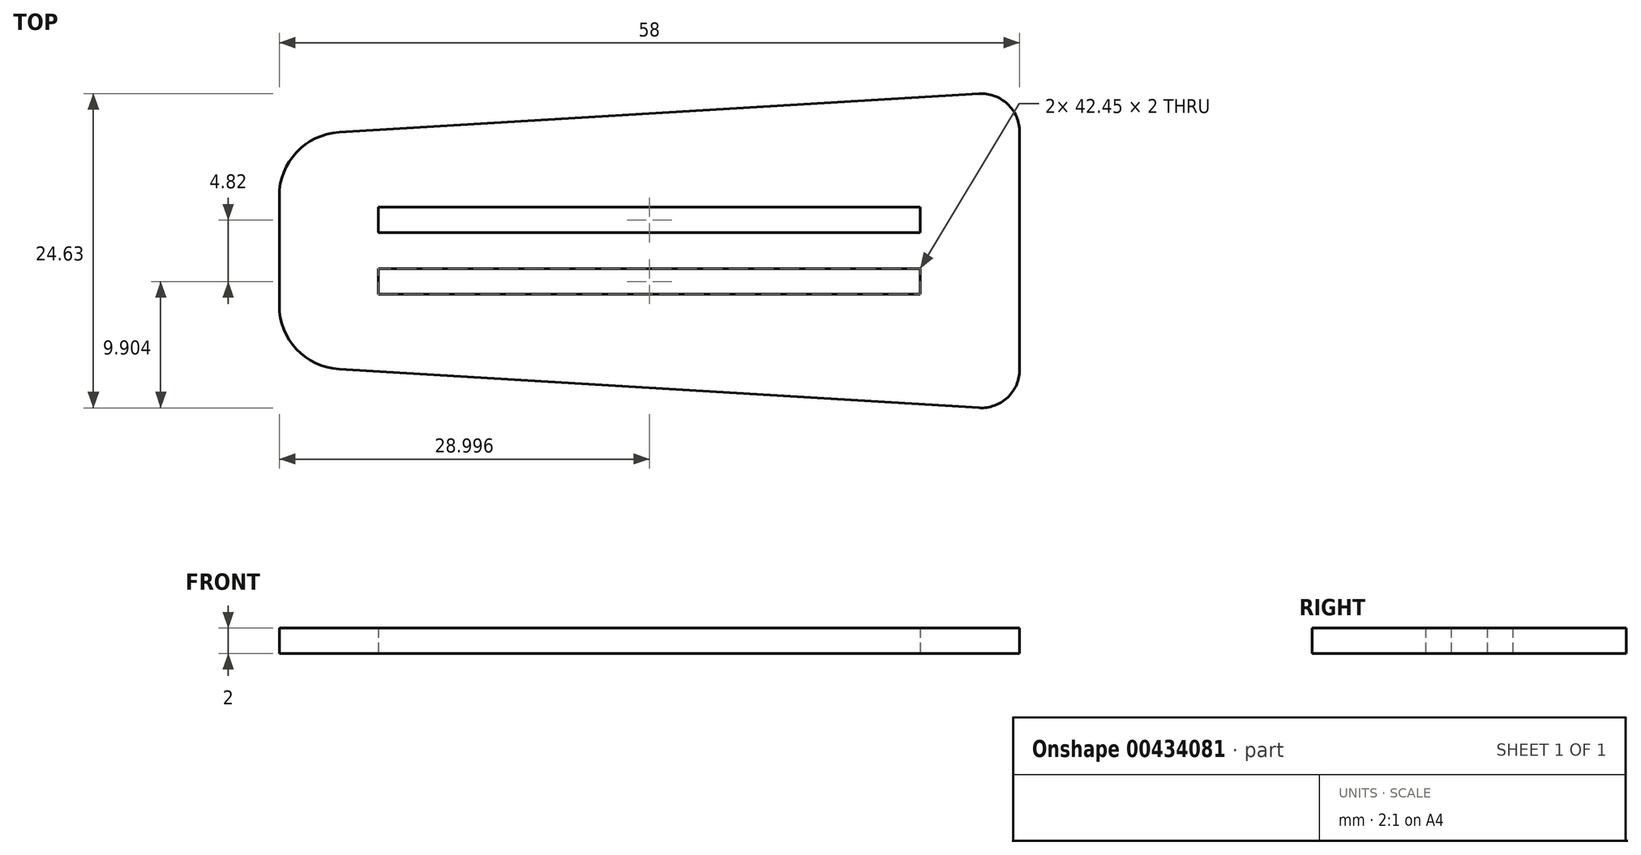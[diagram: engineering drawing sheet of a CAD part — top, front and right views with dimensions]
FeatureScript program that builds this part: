
annotation { "Feature Type Name" : "Feature", "Feature Type Description" : "" }
export const myFeature = defineFeature(function(context is Context, id is Id, definition is map)
    precondition{}
    {
        {
            var Q0;
            Q0=qCreatedBy(makeId("Top.planeOp"),FACE);
            var sketch = newSketch(context, id + "F0", { "sketchPlane" : qUnion([Q0])});
            skLineSegment(sketch, "E0.left", {"start": v(-65.71, 36.47) * mm, "end": v(-65.71, 33.65) * mm});
            skLineSegment(sketch, "E0.right", {"start": v(-7.71, 47.56) * mm, "end": v(-7.71, 22.56) * mm});
            skLineSegment(sketch, "E1", {"start": v(-81.04, 35.06) * mm, "end": v(-57.94, 35.06) * mm, "construction": true});
            skPoint(sketch, "E1.startSnap0", {"position": v(-65.71, 35.06) * mm});
            skLineSegment(sketch, "E2", {"start": v(-36.71, 62.88) * mm, "end": v(-36.71, 8.4) * mm, "construction": true});
            skPoint(sketch, "E2.startSnap0", {"position": v(-36.71, 51.56) * mm});
            skLineSegment(sketch, "E3.0", {"start": v(-57.94, 33.65) * mm, "end": v(-15.49, 33.65) * mm, "construction": true});
            skLineSegment(sketch, "E4.0", {"start": v(-57.94, 36.47) * mm, "end": v(-15.49, 36.47) * mm, "construction": true});
            skLineSegment(sketch, "E5", {"start": v(-57.94, 38.47) * mm, "end": v(-57.94, 36.47) * mm, "construction": true});
            skLineSegment(sketch, "E6.MirrorCS", {"start": v(-15.49, 38.47) * mm, "end": v(-15.49, 36.47) * mm, "construction": true});
            skLineSegment(sketch, "E7.top", {"start": v(-57.94, 38.47) * mm, "end": v(-15.49, 38.47) * mm, "construction": true});
            skLineSegment(sketch, "E7.left", {"start": v(-57.94, 36.47) * mm, "end": v(-57.94, 38.47) * mm, "construction": true});
            skLineSegment(sketch, "E7.right", {"start": v(-15.49, 36.47) * mm, "end": v(-15.49, 38.47) * mm, "construction": true});
            skLineSegment(sketch, "E8.top", {"start": v(-57.94, 33.65) * mm, "end": v(-15.49, 33.65) * mm});
            skLineSegment(sketch, "E9.bottom", {"start": v(-57.94, 38.47) * mm, "end": v(-15.49, 38.47) * mm});
            skLineSegment(sketch, "E9.top", {"start": v(-57.94, 36.47) * mm, "end": v(-15.49, 36.47) * mm});
            skLineSegment(sketch, "E9.left", {"start": v(-57.94, 38.47) * mm, "end": v(-57.94, 36.47) * mm});
            skLineSegment(sketch, "E9.right", {"start": v(-15.49, 38.47) * mm, "end": v(-15.49, 36.47) * mm});
            skLineSegment(sketch, "E10.trimOffspring", {"start": v(-15.49, 35.06) * mm, "end": v(7.2, 35.06) * mm, "construction": true});
            skLineSegment(sketch, "E11.trimOffspring", {"start": v(-57.94, 33.65) * mm, "end": v(-57.94, 31.65) * mm, "construction": true});
            skLineSegment(sketch, "E12.top", {"start": v(-57.94, 31.65) * mm, "end": v(-15.49, 31.65) * mm});
            skLineSegment(sketch, "E12.left", {"start": v(-57.94, 33.65) * mm, "end": v(-57.94, 31.65) * mm});
            skLineSegment(sketch, "E12.right", {"start": v(-15.49, 33.65) * mm, "end": v(-15.49, 31.65) * mm});
            skLineSegment(sketch, "E13", {"start": v(-57.94, 35.06) * mm, "end": v(-15.49, 35.06) * mm, "construction": true});
            skLineSegment(sketch, "E14", {"start": v(-65.71, 35.06) * mm, "end": v(-65.71, 44.06) * mm});
            skPoint(sketch, "E0.bottom.start.orphan", {"position": v(-65.71, 51.56) * mm});
            skPoint(sketch, "E15.orphan", {"position": v(-65.71, 18.56) * mm});
            skLineSegment(sketch, "E16", {"start": v(-65.71, 35.06) * mm, "end": v(-65.71, 26.06) * mm});
            skPoint(sketch, "E17.orphan", {"position": v(-57.94, 26.23) * mm});
            skPoint(sketch, "E18.orphan", {"position": v(-57.94, 42.1) * mm});
            skPoint(sketch, "E19.orphan", {"position": v(-15.49, 42.1) * mm});
            skPoint(sketch, "E20.orphan", {"position": v(-15.49, 26.23) * mm});
            skLineSegment(sketch, "E21.trimOffspring", {"start": v(-15.49, 33.65) * mm, "end": v(-15.49, 31.65) * mm, "construction": true});
            skLineSegment(sketch, "E22.0", {"start": v(-81.04, 26.06) * mm, "end": v(-65.71, 26.06) * mm});
            skLineSegment(sketch, "E23.0", {"start": v(-81.04, 44.06) * mm, "end": v(-65.71, 44.06) * mm});
            skLineSegment(sketch, "E24", {"start": v(-65.71, 44.06) * mm, "end": v(-7.71, 47.56) * mm});
            skPoint(sketch, "E24.endSnap0", {"position": v(-4.15, 47.56) * mm});
            skLineSegment(sketch, "E25", {"start": v(-65.71, 26.06) * mm, "end": v(-7.71, 22.56) * mm});
            skPoint(sketch, "E26.orphan", {"position": v(-7.71, 51.56) * mm});
            skPoint(sketch, "E27.trimOffspring.end.orphan", {"position": v(7.2, 47.56) * mm});
            skPoint(sketch, "E28.MirrorCS.start.orphan", {"position": v(-15.49, 47.56) * mm});
            skPoint(sketch, "E29.orphan", {"position": v(7.2, 22.56) * mm});
            skPoint(sketch, "E30.0.start.orphan", {"position": v(-15.49, 22.56) * mm});
            skPoint(sketch, "E31.orphan", {"position": v(-65.71, 20.56) * mm});
            skPoint(sketch, "E32.MirrorCS.end.orphan", {"position": v(-7.71, 18.56) * mm});
            skPoint(sketch, "E33.orphan", {"position": v(-65.71, 49.56) * mm});
            skSolve(sketch);
        }
        {
            var Q0;
            Q0=makeQuery(id+"F0.imprint","IMPRINT",FACE,{"disambiguationData":[TD([[makeQuery(id+"F0.imprint","IMPRINT",EDGE,{"derivedFrom":sQuery(id+"F0.wireOp",EDGE,"E0.right")}),-1.0]])]});
            extrude(context, id + "F1", {"entities" : qUnion([Q0]), "depth" : 2 * mm, "offsetDistance" : 25 * mm});
        }
        {
            var Q0;
            Q0=makeQuery(id+"F1.opExtrude","SWEPT_EDGE",EDGE,{"disambiguationData":[OSD([sQuery(id+"F0.wireOp",EDGE,"E0.bottom"),sQuery(id+"F0.wireOp",EDGE,"E0.right")])]});
            var Q1;
            Q1=makeQuery(id+"F1.opExtrude","SWEPT_EDGE",EDGE,{"disambiguationData":[OSD([sQuery(id+"F0.wireOp",EDGE,"E0.top"),sQuery(id+"F0.wireOp",EDGE,"E0.left")])]});
            var Q2;
            Q2=makeQuery(id+"F1.opExtrude","SWEPT_EDGE",EDGE,{"disambiguationData":[OSD([sQuery(id+"F0.wireOp",EDGE,"E0.bottom"),sQuery(id+"F0.wireOp",EDGE,"E0.left")])]});
            var Q3;
            Q3=makeQuery(id+"F1.opExtrude","SWEPT_EDGE",EDGE,{"disambiguationData":[OSD([sQuery(id+"F0.wireOp",EDGE,"E0.top"),sQuery(id+"F0.wireOp",EDGE,"E0.right")])]});
            fillet(context, id + "F2", {"entities" : qUnion([Q0, Q1, Q2, Q3]), "radius" : 3 * mm, "tangentPropagation" : true, "allowEdgeOverflow" : false});
        }
        {
            var Q0;
            Q0=makeQuery(id+"F1.opExtrude","SWEPT_EDGE",EDGE,{"disambiguationData":[OSD([sQuery(id+"F0.wireOp",EDGE,"E32.MirrorCS"),sQuery(id+"F0.wireOp",EDGE,"E16")])]});
            var Q1;
            Q1=makeQuery(id+"F1.opExtrude","SWEPT_EDGE",EDGE,{"disambiguationData":[OSD([sQuery(id+"F0.wireOp",EDGE,"E14"),sQuery(id+"F0.wireOp",EDGE,"W7BmLYNM-EGBu-EsTH-d1xR-xXTrqOG5n9p7")])]});
            fillet(context, id + "F3", {"entities" : qUnion([Q0, Q1]), "radius" : 5 * mm, "tangentPropagation" : true, "allowEdgeOverflow" : false});
        }
    });
